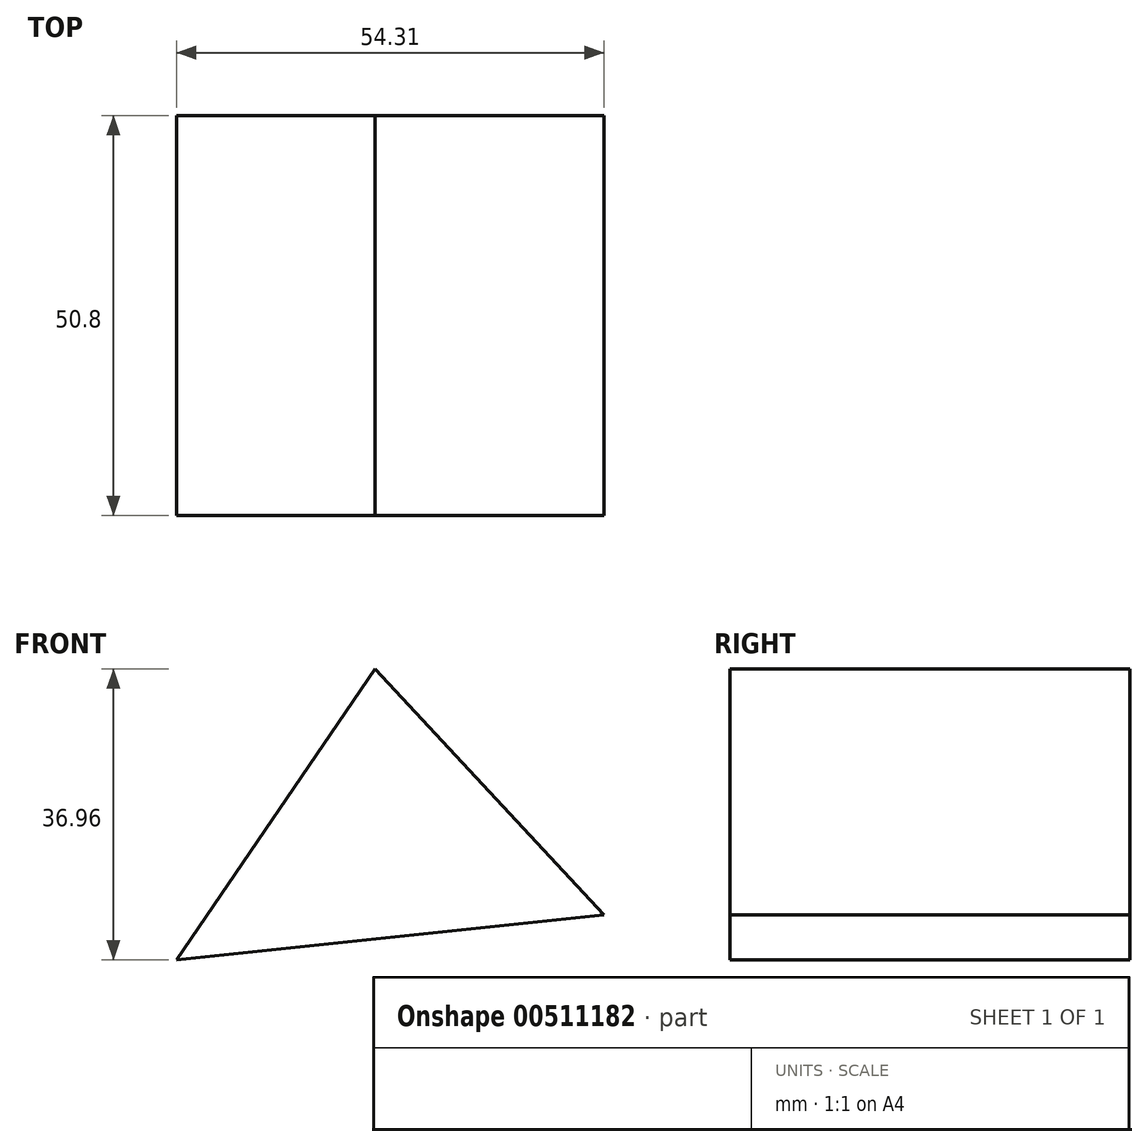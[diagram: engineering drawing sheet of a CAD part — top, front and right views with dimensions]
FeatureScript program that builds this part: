
annotation { "Feature Type Name" : "Feature", "Feature Type Description" : "" }
export const myFeature = defineFeature(function(context is Context, id is Id, definition is map)
    precondition{}
    {
        {
            var Q0;
            Q0=qCreatedBy(makeId("Front.planeOp"),FACE);
            var sketch = newSketch(context, id + "F0", { "sketchPlane" : qUnion([Q0])});
            skLineSegment(sketch, "E0", {"start": v(-43.83, 28.7) * mm, "end": v(-69.03, -8.27) * mm});
            skLineSegment(sketch, "E1", {"start": v(-43.83, 28.7) * mm, "end": v(-14.72, -2.55) * mm});
            skLineSegment(sketch, "E2", {"start": v(-69.03, -8.27) * mm, "end": v(-14.72, -2.55) * mm});
            skLineSegment(sketch, "E3", {"start": v(-43.83, 28.7) * mm, "end": v(-40.24, -5.4) * mm});
            skPoint(sketch, "E3.endSnap0", {"position": v(-41.88, -5.4) * mm});
            skSolve(sketch);
        }
        {
            var Q0;
            {var subQ0=sQuery(id+"F0.wireOp",EDGE,"E0");Q0=makeQuery(id+"F0.imprint","IMPRINT",FACE,{"disambiguationData":[TD([[makeQuery(id+"F0.imprint","IMPRINT",EDGE,{"derivedFrom":subQ0}),1.0]])]});}
            var Q1;
            {var subQ0=sQuery(id+"F0.wireOp",EDGE,"E1");Q1=makeQuery(id+"F0.imprint","IMPRINT",FACE,{"disambiguationData":[TD([[makeQuery(id+"F0.imprint","IMPRINT",EDGE,{"derivedFrom":subQ0}),-1.0]])]});}
            extrude(context, id + "F1", {"entities" : qUnion([Q0, Q1]), "oppositeDirection" : true, "depth" : 76.2 * mm, "hasSecondDirection" : true, "secondDirectionOppositeDirection" : true, "secondDirectionDepth" : 25.4 * mm});
        }
    });
